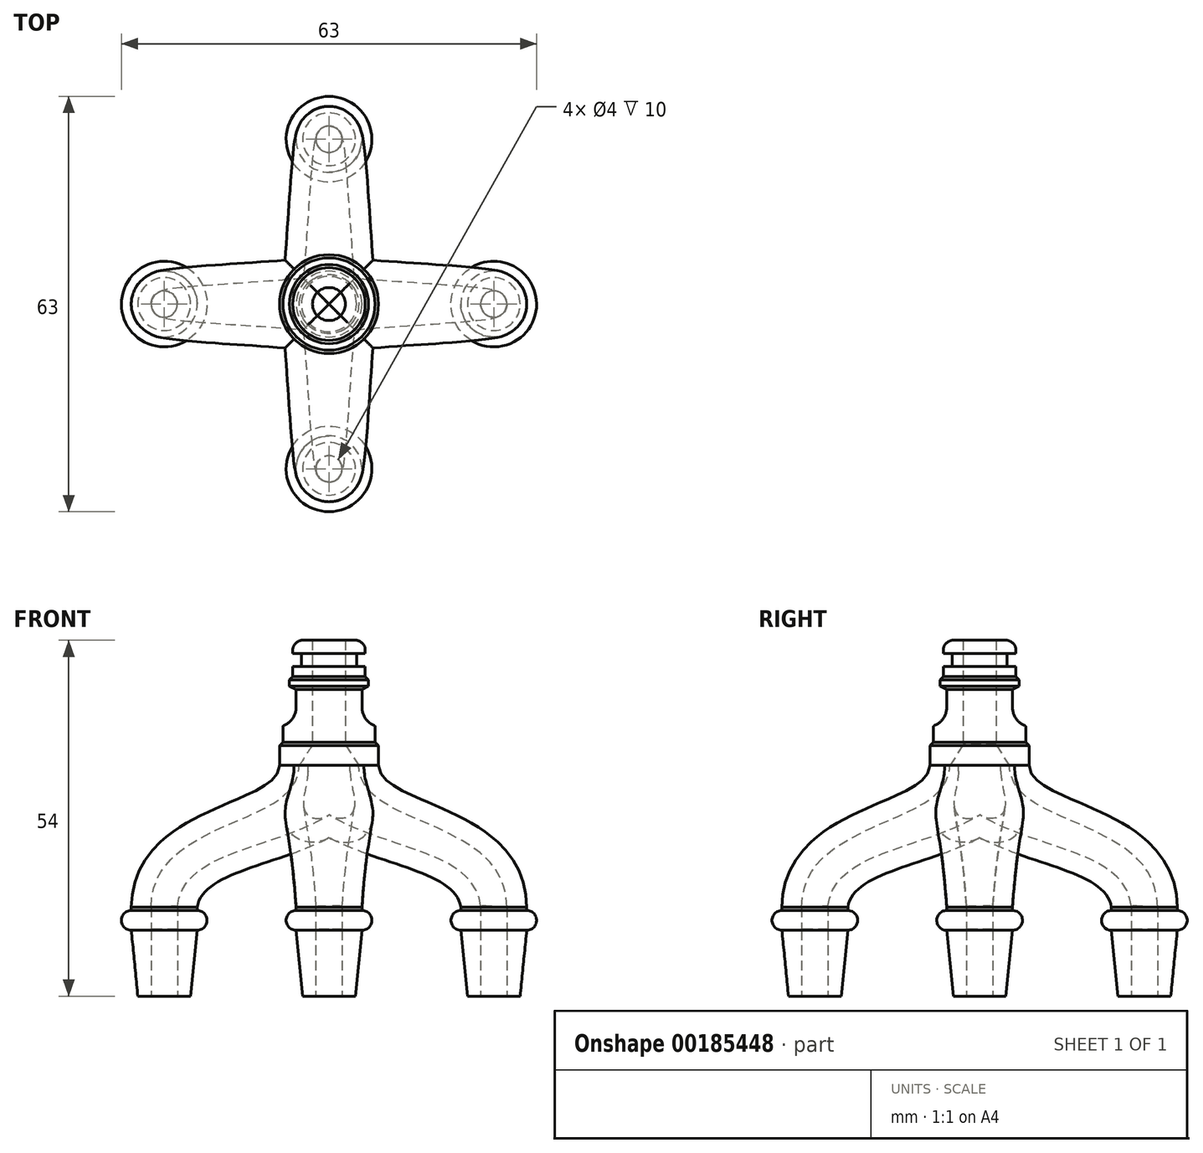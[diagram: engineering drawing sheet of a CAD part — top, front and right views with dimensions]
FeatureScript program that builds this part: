
annotation { "Feature Type Name" : "Feature", "Feature Type Description" : "" }
export const myFeature = defineFeature(function(context is Context, id is Id, definition is map)
    precondition{}
    {
        {
            var Q0;
            Q0=qCreatedBy(makeId("Front.planeOp"),FACE);
            var sketch = newSketch(context, id + "F0", { "sketchPlane" : qUnion([Q0])});
            skLineSegment(sketch, "E0", {"start": v(-25, 0) * mm, "end": v(-25, 13.5) * mm});
            skLineSegment(sketch, "E1", {"start": v(-25, 0) * mm, "end": v(-29, 0) * mm});
            skLineSegment(sketch, "E2", {"start": v(-29, 0) * mm, "end": v(-30, 10) * mm});
            skLineSegment(sketch, "E3", {"start": v(-30, 13) * mm, "end": v(-30, 13.5) * mm});
            skArc(sketch, "E4", {"start": v(-30, 13) * mm, "mid": v(-31.5, 11.5) * mm, "end": v(-30, 10) * mm});
            skLineSegment(sketch, "E5", {"start": v(-30, 13.5) * mm, "end": v(-25, 13.5) * mm});
            skSolve(sketch);
        }
        {
            var Q0;
            Q0=makeQuery(id+"F0.imprint","IMPRINT",FACE,{"disambiguationData":[TD([[makeQuery(id+"F0.imprint","IMPRINT",EDGE,{"derivedFrom":sQuery(id+"F0.wireOp",EDGE,"E0")}),1.0]])]});
            var Q1;
            Q1=sQuery(id+"F0.wireOp",EDGE,"E0");
            revolve(context, id + "F1", {"entities" : qUnion([Q0]), "axis" : qUnion([Q1]), "revolveType" : RevolveType.FULL});
        }
        {
            var Q0;
            Q0=qCreatedBy(makeId("Top.planeOp"),FACE);
            cPlane(context, id + "F2", {"entities" : qUnion([Q0]), "cplaneType" : CPlaneType.OFFSET, "offset" : 35 * mm, "width" : 150 * mm, "height" : 150 * mm});
        }
        {
            var Q0;
            Q0=qCreatedBy(id+"F2.planeOp",FACE);
            var sketch = newSketch(context, id + "F3", { "sketchPlane" : qUnion([Q0])});
            skCircle(sketch, "E6", {"center": v(0, 0) * mm, "radius": 7.5 * mm});
            skLineSegment(sketch, "E7", {"start": v(0, 0) * mm, "end": v(7.5, 0) * mm, "construction": true});
            skLineSegment(sketch, "E8", {"start": v(0, 0) * mm, "end": v(-7.5, 0) * mm, "construction": true});
            skSolve(sketch);
        }
        {
            var Q0;
            Q0=makeQuery(id+"F1.opRevolve","SWEPT_FACE",FACE,{"disambiguationData":[OSD([sQuery(id+"F0.wireOp",EDGE,"E5")])]});
            var sketch = newSketch(context, id + "F4", { "sketchPlane" : qUnion([Q0])});
            skCircle(sketch, "E9", {"center": v(-25, 0) * mm, "radius": 5 * mm});
            skLineSegment(sketch, "E10", {"start": v(-25, 0) * mm, "end": v(-20, 0) * mm, "construction": true});
            skLineSegment(sketch, "E11", {"start": v(-25, 0) * mm, "end": v(-30, 0) * mm, "construction": true});
            skSolve(sketch);
        }
        {
            var Q0;
            Q0=qCreatedBy(makeId("Front.planeOp"),FACE);
            var sketch = newSketch(context, id + "F5", { "sketchPlane" : qUnion([Q0])});
            skFitSpline(sketch, "E12", {"points": [v(-20, 13.5) * mm, v(7.5, 35) * mm], "startDerivative": vector(3.16, 24.67) * mm, "endDerivative": vector(-0.57, 46.13) * mm});
            skFitSpline(sketch, "E13", {"points": [v(-30, 13.5) * mm, v(-7.5, 35) * mm], "startDerivative": vector(0.6, 46.56) * mm, "endDerivative": vector(0.95, 18.76) * mm});
            skSolve(sketch);
        }
        {
            var Q1;
            Q1=makeQuery(id+"F4.imprint","IMPRINT",FACE,{"disambiguationData":[TD([[makeQuery(id+"F4.imprint","IMPRINT",EDGE,{"derivedFrom":sQuery(id+"F4.wireOp",EDGE,"E9")}),-1.0]])]});
            var Q2;
            Q2=makeQuery(id+"F3.imprint","IMPRINT",FACE,{"disambiguationData":[TD([[makeQuery(id+"F3.imprint","IMPRINT",EDGE,{"derivedFrom":sQuery(id+"F3.wireOp",EDGE,"E6")}),1.0]])]});
            var Q3;
            Q3=sQuery(id+"F5.wireOp",EDGE,"E12");
            var Q4;
            Q4=sQuery(id+"F5.wireOp",EDGE,"E13");
            loft(context, id + "F6", {"operationType" : NewBodyOperationType.ADD, "addGuides" : true, "sheetProfilesArray" : [{ "sheetProfileEntities" : qUnion([Q1]) }, { "sheetProfileEntities" : qUnion([Q2]) }], "guidesArray" : [{ "guideEntities" : qUnion([Q3]), "guideDerivativeType" : LoftGuideDerivativeType.DEFAULT, "guideDerivativeMagnitude" : 1 }, { "guideEntities" : qUnion([Q4]), "guideDerivativeType" : LoftGuideDerivativeType.DEFAULT, "guideDerivativeMagnitude" : 1 }]});
        }
        {
            var Q0;
            Q0=qCreatedBy(makeId("Front.planeOp"),FACE);
            var sketch = newSketch(context, id + "F7", { "sketchPlane" : qUnion([Q0])});
            skLineSegment(sketch, "E14", {"start": v(0, 35) * mm, "end": v(0, 71.57) * mm, "construction": true});
            skSolve(sketch);
        }
        {
            var Q0;
            Q0=makeQuery(id+"F1.opRevolve","SWEPT_BODY",BODY,{"disambiguationData":[OSD([sQuery(id+"F0.wireOp",EDGE,"E0"),sQuery(id+"F0.wireOp",EDGE,"E1"),sQuery(id+"F0.wireOp",EDGE,"E2"),sQuery(id+"F0.wireOp",EDGE,"E3"),sQuery(id+"F0.wireOp",EDGE,"E4"),sQuery(id+"F0.wireOp",EDGE,"E5")])]});
            var Q1;
            Q1=sQuery(id+"F7.wireOp",EDGE,"E14");
            transform(context, id + "F8", {"entities" : qUnion([Q0]), "transformType" : TransformType.ROTATION, "transformAxis" : qUnion([Q1]), "angle" : 90 * degree, "makeCopy" : true});
        }
        {
            var Q0;
            Q0=makeQuery(id+"F1.opRevolve","SWEPT_BODY",BODY,{"disambiguationData":[OSD([sQuery(id+"F0.wireOp",EDGE,"E0"),sQuery(id+"F0.wireOp",EDGE,"E1"),sQuery(id+"F0.wireOp",EDGE,"E2"),sQuery(id+"F0.wireOp",EDGE,"E3"),sQuery(id+"F0.wireOp",EDGE,"E4"),sQuery(id+"F0.wireOp",EDGE,"E5")])]});
            var Q1;
            Q1=makeQuery(id+"F8.opPattern","COPY",BODY,{"derivedFrom":makeQuery(id+"F1.opRevolve","SWEPT_BODY",BODY,{"disambiguationData":[OSD([sQuery(id+"F0.wireOp",EDGE,"E0"),sQuery(id+"F0.wireOp",EDGE,"E1"),sQuery(id+"F0.wireOp",EDGE,"E2"),sQuery(id+"F0.wireOp",EDGE,"E3"),sQuery(id+"F0.wireOp",EDGE,"E4"),sQuery(id+"F0.wireOp",EDGE,"E5")])]}),"instanceName":"1"});
            booleanBodies(context, id + "F9", {"operationType" : BooleanOperationType.UNION, "tools" : qUnion([Q0, Q1])});
        }
        {
            var Q0;
            Q0=makeQuery(id+"F1.opRevolve","SWEPT_BODY",BODY,{"disambiguationData":[OSD([sQuery(id+"F0.wireOp",EDGE,"E0"),sQuery(id+"F0.wireOp",EDGE,"E1"),sQuery(id+"F0.wireOp",EDGE,"E2"),sQuery(id+"F0.wireOp",EDGE,"E3"),sQuery(id+"F0.wireOp",EDGE,"E4"),sQuery(id+"F0.wireOp",EDGE,"E5")])]});
            var Q1;
            Q1=sQuery(id+"F7.wireOp",EDGE,"E14");
            transform(context, id + "F10", {"entities" : qUnion([Q0]), "transformType" : TransformType.ROTATION, "transformAxis" : qUnion([Q1]), "angle" : 180 * degree, "makeCopy" : true});
        }
        {
            var Q0;
            Q0=makeQuery(id+"F1.opRevolve","SWEPT_BODY",BODY,{"disambiguationData":[OSD([sQuery(id+"F0.wireOp",EDGE,"E0"),sQuery(id+"F0.wireOp",EDGE,"E1"),sQuery(id+"F0.wireOp",EDGE,"E2"),sQuery(id+"F0.wireOp",EDGE,"E3"),sQuery(id+"F0.wireOp",EDGE,"E4"),sQuery(id+"F0.wireOp",EDGE,"E5")])]});
            var Q1;
            Q1=makeQuery(id+"F10.opPattern","COPY",BODY,{"derivedFrom":makeQuery(id+"F1.opRevolve","SWEPT_BODY",BODY,{"disambiguationData":[OSD([sQuery(id+"F0.wireOp",EDGE,"E0"),sQuery(id+"F0.wireOp",EDGE,"E1"),sQuery(id+"F0.wireOp",EDGE,"E2"),sQuery(id+"F0.wireOp",EDGE,"E3"),sQuery(id+"F0.wireOp",EDGE,"E4"),sQuery(id+"F0.wireOp",EDGE,"E5")])]}),"instanceName":"1"});
            booleanBodies(context, id + "F11", {"operationType" : BooleanOperationType.UNION, "tools" : qUnion([Q0, Q1])});
        }
        {
            var Q0;
            Q0=makeQuery(id+"F6.opLoft","CAP_FACE",FACE,{"disambiguationData":[OSD([makeQuery(id+"F3.imprint","IMPRINT",FACE,{"disambiguationData":[TD([[makeQuery(id+"F3.imprint","IMPRINT",EDGE,{"derivedFrom":sQuery(id+"F3.wireOp",EDGE,"E6")}),1.0]])]})])],"isStart":true});
            shell(context, id + "F12", {"entities" : qUnion([Q0]), "thickness" : 3 * mm});
        }
        {
            var Q0;
            Q0=makeQuery(id+"F8.opPattern","COPY",FACE,{"derivedFrom":makeQuery(id+"F1.opRevolve","SWEPT_FACE",FACE,{"disambiguationData":[OSD([sQuery(id+"F0.wireOp",EDGE,"E1")])]}),"instanceName":"1"});
            var sketch = newSketch(context, id + "F13", { "sketchPlane" : qUnion([Q0])});
            skCircle(sketch, "E15", {"center": v(0, 25) * mm, "radius": 2 * mm});
            skSolve(sketch);
        }
        {
            var Q0;
            Q0=makeQuery(id+"F13.imprint","IMPRINT",FACE,{"disambiguationData":[TD([[makeQuery(id+"F13.imprint","IMPRINT",EDGE,{"derivedFrom":sQuery(id+"F13.wireOp",EDGE,"E15")}),1.0]])]});
            extrude(context, id + "F14", {"entities" : qUnion([Q0]), "operationType" : NewBodyOperationType.REMOVE, "oppositeDirection" : true, "depth" : 10 * mm});
        }
        {
            var Q0;
            Q0=makeQuery(id+"F10.opPattern","COPY",FACE,{"derivedFrom":makeQuery(id+"F1.opRevolve","SWEPT_FACE",FACE,{"disambiguationData":[OSD([sQuery(id+"F0.wireOp",EDGE,"E1")])]}),"instanceName":"1"});
            var sketch = newSketch(context, id + "F15", { "sketchPlane" : qUnion([Q0])});
            skCircle(sketch, "E16", {"center": v(25, 0) * mm, "radius": 2 * mm});
            skSolve(sketch);
        }
        {
            var Q0;
            Q0=makeQuery(id+"F15.imprint","IMPRINT",FACE,{"disambiguationData":[TD([[makeQuery(id+"F15.imprint","IMPRINT",EDGE,{"derivedFrom":sQuery(id+"F15.wireOp",EDGE,"E16")}),1.0]])]});
            extrude(context, id + "F16", {"entities" : qUnion([Q0]), "operationType" : NewBodyOperationType.REMOVE, "oppositeDirection" : true, "depth" : 10 * mm});
        }
        {
            var Q0;
            Q0=makeQuery(id+"F10.opPattern","COPY",FACE,{"derivedFrom":makeQuery(id+"F8.opPattern","COPY",FACE,{"derivedFrom":makeQuery(id+"F1.opRevolve","SWEPT_FACE",FACE,{"disambiguationData":[OSD([sQuery(id+"F0.wireOp",EDGE,"E1")])]}),"instanceName":"1"}),"instanceName":"1"});
            var sketch = newSketch(context, id + "F17", { "sketchPlane" : qUnion([Q0])});
            skCircle(sketch, "E17", {"center": v(0, -25) * mm, "radius": 2 * mm});
            skSolve(sketch);
        }
        {
            var Q0;
            Q0=makeQuery(id+"F17.imprint","IMPRINT",FACE,{"disambiguationData":[TD([[makeQuery(id+"F17.imprint","IMPRINT",EDGE,{"derivedFrom":sQuery(id+"F17.wireOp",EDGE,"E17")}),1.0]])]});
            extrude(context, id + "F18", {"entities" : qUnion([Q0]), "operationType" : NewBodyOperationType.REMOVE, "oppositeDirection" : true, "depth" : 10 * mm});
        }
        {
            var Q0;
            Q0=makeQuery(id+"F1.opRevolve","SWEPT_FACE",FACE,{"disambiguationData":[OSD([sQuery(id+"F0.wireOp",EDGE,"E1")])]});
            var sketch = newSketch(context, id + "F19", { "sketchPlane" : qUnion([Q0])});
            skCircle(sketch, "E18", {"center": v(-25, 0) * mm, "radius": 2 * mm});
            skSolve(sketch);
        }
        {
            var Q0;
            Q0=makeQuery(id+"F19.imprint","IMPRINT",FACE,{"disambiguationData":[TD([[makeQuery(id+"F19.imprint","IMPRINT",EDGE,{"derivedFrom":sQuery(id+"F19.wireOp",EDGE,"E18")}),1.0]])]});
            extrude(context, id + "F20", {"entities" : qUnion([Q0]), "operationType" : NewBodyOperationType.REMOVE, "oppositeDirection" : true, "depth" : 10 * mm});
        }
        {
            var Q0;
            Q0=qCreatedBy(makeId("Front.planeOp"),FACE);
            var sketch = newSketch(context, id + "F21", { "sketchPlane" : qUnion([Q0])});
            skLineSegment(sketch, "E19", {"start": v(-7.5, 35) * mm, "end": v(-7.5, 38) * mm});
            skLineSegment(sketch, "E20", {"start": v(-7.5, 38) * mm, "end": v(-7, 38) * mm});
            skLineSegment(sketch, "E21", {"start": v(-7, 38) * mm, "end": v(-7, 41) * mm});
            skLineSegment(sketch, "E22", {"start": v(-7, 41) * mm, "end": v(-5, 41) * mm});
            skLineSegment(sketch, "E23", {"start": v(-5, 41) * mm, "end": v(-5, 47) * mm});
            skLineSegment(sketch, "E24", {"start": v(-5, 47) * mm, "end": v(-6, 47) * mm});
            skLineSegment(sketch, "E25", {"start": v(-6, 47) * mm, "end": v(-6, 48) * mm});
            skLineSegment(sketch, "E26", {"start": v(-6, 48) * mm, "end": v(-5.5, 48) * mm});
            skLineSegment(sketch, "E27", {"start": v(-5.5, 48) * mm, "end": v(-5.5, 50) * mm});
            skLineSegment(sketch, "E28", {"start": v(-5.5, 50) * mm, "end": v(-4.19, 50) * mm});
            skLineSegment(sketch, "E29", {"start": v(-4.19, 50) * mm, "end": v(-4.19, 52) * mm});
            skLineSegment(sketch, "E30", {"start": v(-4.19, 52) * mm, "end": v(-5.5, 52) * mm});
            skLineSegment(sketch, "E31", {"start": v(-5.5, 52) * mm, "end": v(-5.5, 54) * mm});
            skLineSegment(sketch, "E32", {"start": v(-5.5, 54) * mm, "end": v(-2.5, 54) * mm});
            skLineSegment(sketch, "E33", {"start": v(-2.5, 54) * mm, "end": v(-2.5, 38.13) * mm});
            skLineSegment(sketch, "E34", {"start": v(-2.5, 38.13) * mm, "end": v(-4.5, 35) * mm});
            skPoint(sketch, "E35.orphan", {"position": v(0, 54) * mm});
            skLineSegment(sketch, "E36", {"start": v(-4.5, 35) * mm, "end": v(-7.5, 35) * mm});
            skSolve(sketch);
        }
        {
            var Q0;
            Q0=makeQuery(id+"F21.imprint","IMPRINT",FACE,{"disambiguationData":[TD([[makeQuery(id+"F21.imprint","IMPRINT",EDGE,{"derivedFrom":sQuery(id+"F21.wireOp",EDGE,"E19")}),-1.0]])]});
            var Q1;
            Q1=sQuery(id+"F7.wireOp",EDGE,"E14");
            revolve(context, id + "F22", {"operationType" : NewBodyOperationType.ADD, "entities" : qUnion([Q0]), "axis" : qUnion([Q1]), "revolveType" : RevolveType.FULL});
        }
        {
            var Q0;
            Q0=makeQuery(id+"F22.opRevolve","SWEPT_EDGE",EDGE,{"disambiguationData":[OSD([sQuery(id+"F21.wireOp",EDGE,"E31"),sQuery(id+"F21.wireOp",EDGE,"E32")])]});
            fillet(context, id + "F23", {"entities" : qUnion([Q0]), "radius" : 1.5 * mm, "tangentPropagation" : true, "allowEdgeOverflow" : false});
        }
        {
            var Q0;
            Q0=makeQuery(id+"F22.opRevolve","SWEPT_EDGE",EDGE,{"disambiguationData":[OSD([sQuery(id+"F21.wireOp",EDGE,"E26"),sQuery(id+"F21.wireOp",EDGE,"E27")])]});
            chamfer(context, id + "F24", {"entities" : qUnion([Q0]), "width" : 0.5 * mm, "tangentPropagation" : true});
        }
        {
            var Q0;
            Q0=makeQuery(id+"F22.opRevolve","SWEPT_EDGE",EDGE,{"disambiguationData":[OSD([sQuery(id+"F21.wireOp",EDGE,"E23"),sQuery(id+"F21.wireOp",EDGE,"E24")])]});
            chamfer(context, id + "F25", {"entities" : qUnion([Q0]), "chamferType" : ChamferType.TWO_OFFSETS, "width1" : 0.5 * mm, "oppositeDirection" : false, "width2" : 1 * mm, "tangentPropagation" : true});
        }
        {
            var Q0;
            Q0=makeQuery(id+"F22.opRevolve","SWEPT_EDGE",EDGE,{"disambiguationData":[OSD([sQuery(id+"F21.wireOp",EDGE,"E22"),sQuery(id+"F21.wireOp",EDGE,"E23")])]});
            fillet(context, id + "F26", {"entities" : qUnion([Q0]), "radius" : 3 * mm, "tangentPropagation" : true, "allowEdgeOverflow" : false});
        }
        {
            var Q0;
            Q0=makeQuery(id+"F22.opRevolve","SWEPT_EDGE",EDGE,{"disambiguationData":[OSD([sQuery(id+"F21.wireOp",EDGE,"E20"),sQuery(id+"F21.wireOp",EDGE,"E21")])]});
            chamfer(context, id + "F27", {"entities" : qUnion([Q0]), "width" : 0.5 * mm, "tangentPropagation" : true});
        }
        {
            var Q0;
            Q0=makeQuery(id+"F26.opFillet","BLEND_EDGE",EDGE,{"blendedFrom":[makeQuery(id+"F22.opRevolve","SWEPT_EDGE",EDGE,{"disambiguationData":[OSD([sQuery(id+"F21.wireOp",EDGE,"E22"),sQuery(id+"F21.wireOp",EDGE,"E23")])]}),makeQuery(id+"F22.opRevolve","SWEPT_FACE",FACE,{"disambiguationData":[OSD([sQuery(id+"F21.wireOp",EDGE,"E21")])]})],"blendedInto":[makeQuery(id+"F22.opRevolve","SWEPT_FACE",FACE,{"disambiguationData":[OSD([sQuery(id+"F21.wireOp",EDGE,"E21")])]})]});
            fillet(context, id + "F28", {"entities" : qUnion([Q0]), "radius" : 0.2 * mm, "tangentPropagation" : true, "allowEdgeOverflow" : false});
        }
    });
